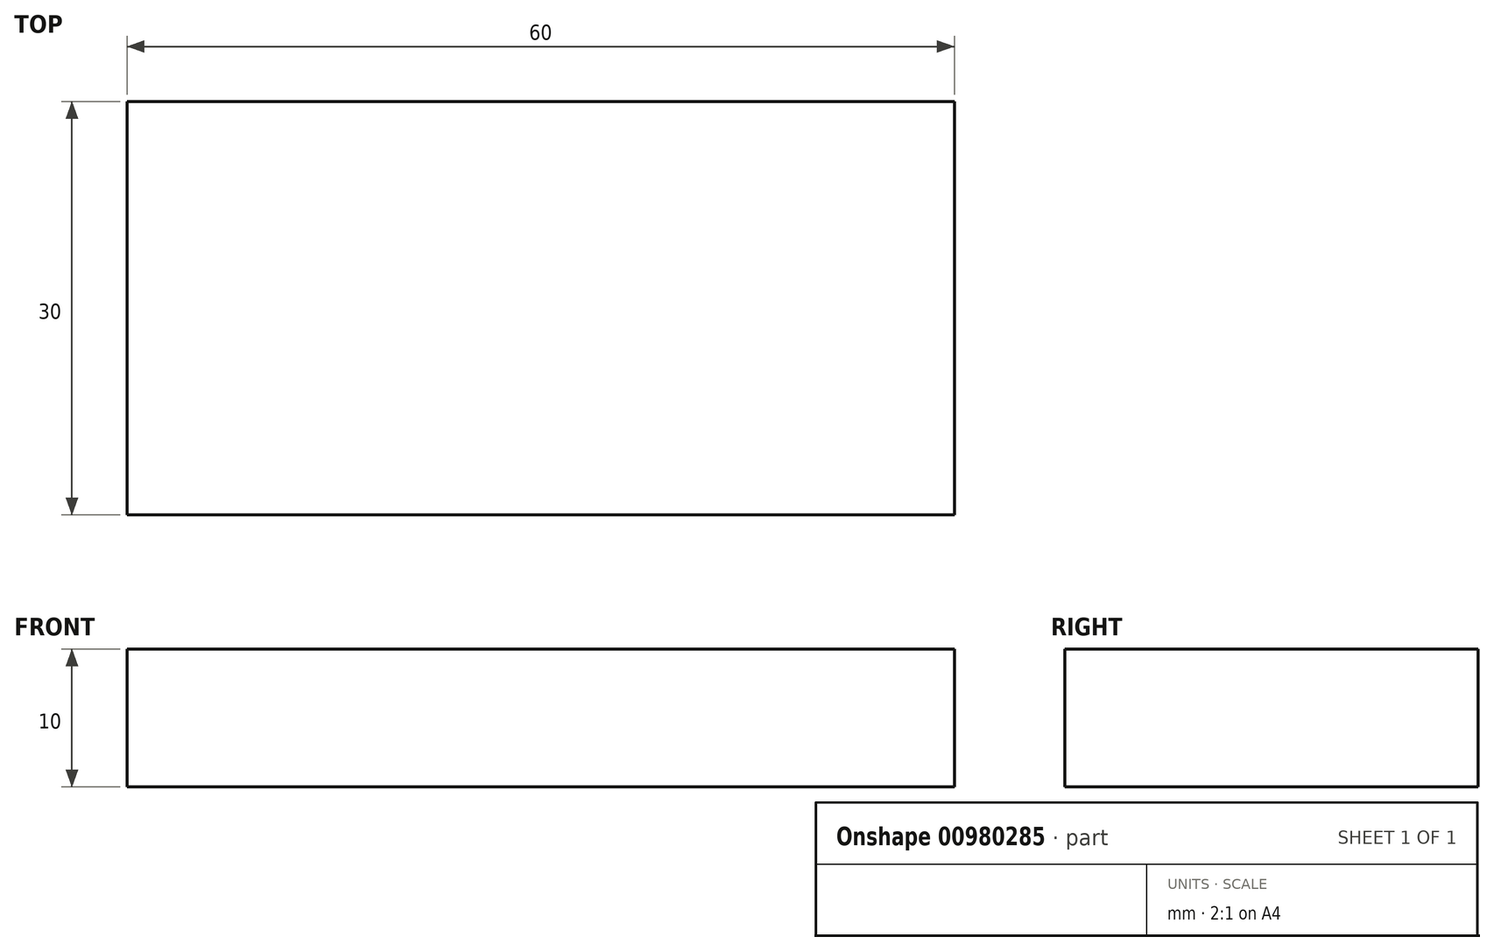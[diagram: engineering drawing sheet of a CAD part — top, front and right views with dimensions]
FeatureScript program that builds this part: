
annotation { "Feature Type Name" : "Feature", "Feature Type Description" : "" }
export const myFeature = defineFeature(function(context is Context, id is Id, definition is map)
    precondition{}
    {
        {
            assignVariable(context, id + "F0", {"name" : "Height", "anyValue" : 10});
        }
        {
            var Q0;
            Q0=qCreatedBy(makeId("Top.planeOp"),FACE);
            var sketch = newSketch(context, id + "F1", { "sketchPlane" : qUnion([Q0])});
            skLineSegment(sketch, "E0.bottom", {"start": v(30, 15) * mm, "end": v(-30, 15) * mm});
            skLineSegment(sketch, "E0.top", {"start": v(30, -15) * mm, "end": v(-30, -15) * mm});
            skLineSegment(sketch, "E0.left", {"start": v(30, 15) * mm, "end": v(30, -15) * mm});
            skLineSegment(sketch, "E0.right", {"start": v(-30, 15) * mm, "end": v(-30, -15) * mm});
            skPoint(sketch, "E0.middle", {"position": v(0, 0) * mm});
            skSolve(sketch);
        }
        {
            var Q0;
            Q0 = qSketchRegion(id + "F1", true);
            extrude(context, id + "F2", {"entities" : qUnion([Q0]), "depth" : (getVariable(context, 'Height')) * mm, "offsetDistance" : 25 * mm});
        }
    });
